# Revit family: 3631603_3631613_MAST 7.0M Ø76 PL160
name_source: partatom
category: Lighting Fixtures
units: mm (PartAtom-declared; Revit-internal decimal feet)

## family parameters
Always vertical = Yes
Cut with Voids When Loaded = No
Light Source = No
Maintain Annotation Orientation = No
OmniClass Number = 23.80.70.14.21
OmniClass Title = Street and Roadway Lighting
Part Type = Normal
Room Calculation Point = No
Round Connector Dimension = Use Diameter
Shared = No
Work Plane-Based = No

## types (1)
- Avtrappede master
    Area = 4,71 m²
    Art.nr = 3631603/3631613
    Art.nr CombiCoat = 3631613
    Art.nr VZN = 3631603
    Bunndiameter = Ø140
    CE-godkjent = Ja
    Category = Avtrappede master
    Center of Gravity = X: -0,004 mm Y: 1,543 mm Z: 2907,387 mm
    Default Elevation = 0 mm  [stored 0 ft]
    Density = 7580,09 kg/m³
    Description = MAST 7.0M Ø76 PL160
    Design Status = 1
    Designer = khk
    EL nr CombiCoat = 3631613
    El nr = 3640106/3640118
    El nr VZN = 3631603
    Filnamn-VO = Standard
    Filnavn = MAST 7.0M Ø76 PL160
    Fotplate C/C bolter = 160mm
    Fundament = 3520160C
    Lyspunkthoyde = 7m
    Manufacturer = Vik Ørsta AS
    Mass = 62,31 kg
    Model = 3631603_3631613
    Part Number = L10184
    Requested Accuracy = Low
    Revision Number = -
    Size = 0,0,0
    Sti&Filnamn-VO = Standard
    Title = MAST 7.0M Ø76 PL160
    Toppdiameter = Ø76
    Volume = 0,01 m³

note: [stored X ft] marks values corroborated as IEEE doubles in the binary element streams (Revit-internal decimal feet)

## geometry (parser evidence)
native form markers: Sweep x2
no freeform markers — native parametric forms only
